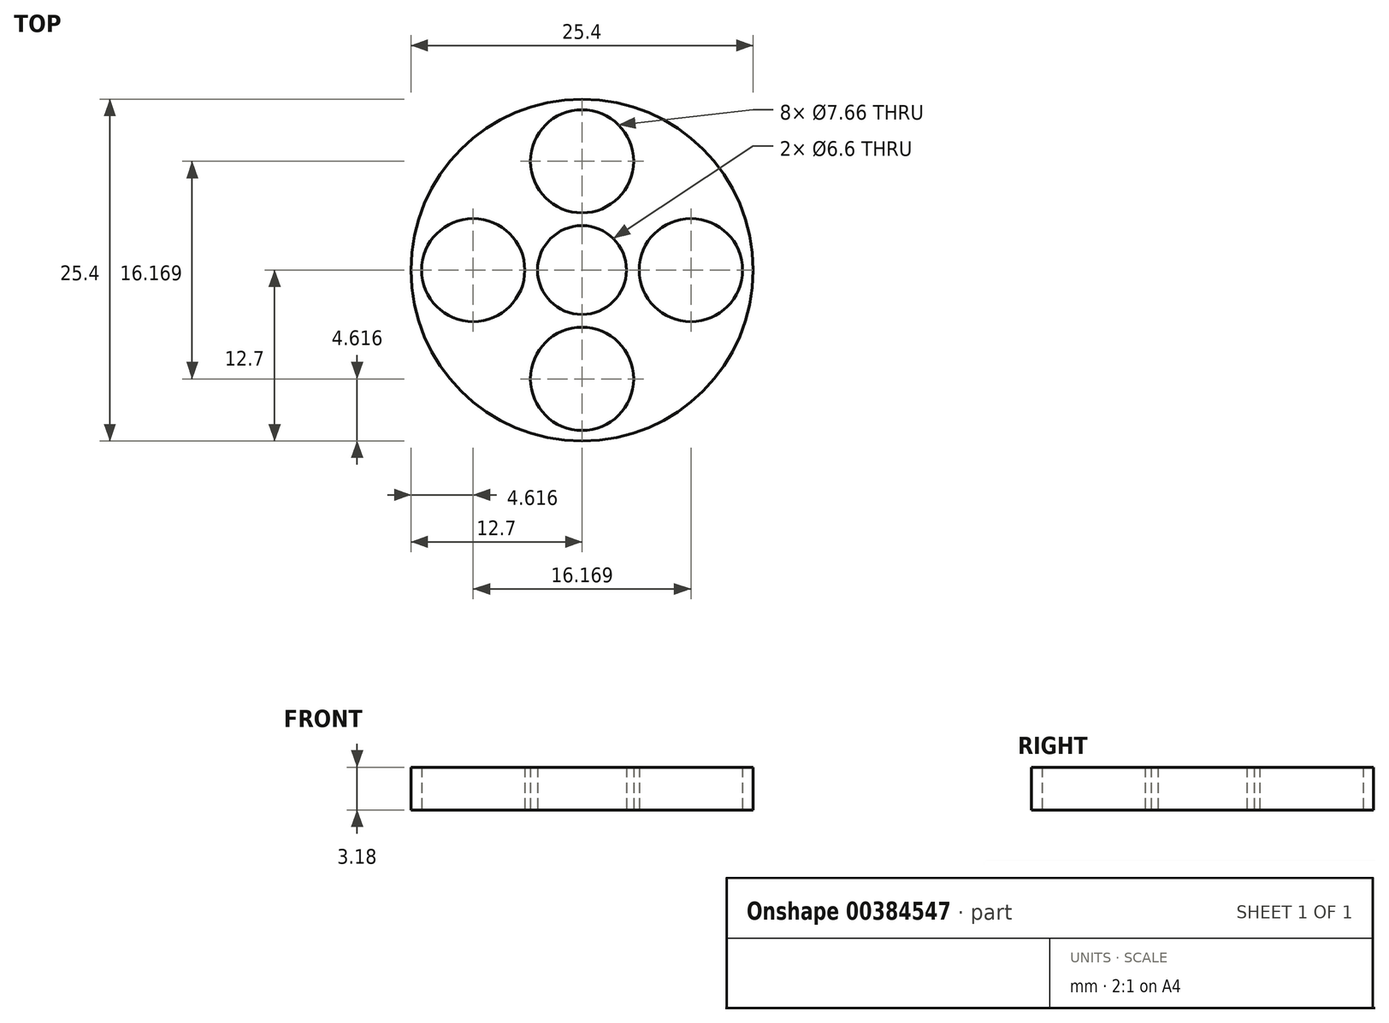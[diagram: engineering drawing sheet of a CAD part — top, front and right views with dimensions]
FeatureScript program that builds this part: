
annotation { "Feature Type Name" : "Feature", "Feature Type Description" : "" }
export const myFeature = defineFeature(function(context is Context, id is Id, definition is map)
    precondition{}
    {
        {
            var Q0;
            Q0=qCreatedBy(makeId("Top.planeOp"),FACE);
            var sketch = newSketch(context, id + "F0", { "sketchPlane" : qUnion([Q0])});
            skCircle(sketch, "E0", {"center": v(0, 0) * mm, "radius": 12.7 * mm});
            skSolve(sketch);
        }
        {
            var Q0;
            Q0=makeQuery(id+"F0.imprint","IMPRINT",FACE,{"disambiguationData":[TD([[makeQuery(id+"F0.imprint","IMPRINT",EDGE,{"derivedFrom":sQuery(id+"F0.wireOp",EDGE,"E0")}),1.0]])]});
            extrude(context, id + "F1", {"entities" : qUnion([Q0]), "depth" : 3.17 * mm});
        }
        {
            var Q0;
            Q0=qCreatedBy(makeId("Top.planeOp"),FACE);
            var sketch = newSketch(context, id + "F2", { "sketchPlane" : qUnion([Q0])});
            skCircle(sketch, "E1", {"center": v(0, 0) * mm, "radius": 3.3 * mm});
            skSolve(sketch);
        }
        {
            var Q0;
            Q0 = qSketchRegion(id + "F2", true);
            extrude(context, id + "F3", {"entities" : qUnion([Q0]), "operationType" : NewBodyOperationType.REMOVE, "depth" : 25.4 * mm});
        }
        {
            var Q0;
            Q0=qCreatedBy(makeId("Top.planeOp"),FACE);
            var sketch = newSketch(context, id + "F4", { "sketchPlane" : qUnion([Q0])});
            skCircle(sketch, "E2", {"center": v(0, 8.08) * mm, "radius": 3.83 * mm});
            skCircle(sketch, "E3.1.0", {"center": v(-8.08, 0) * mm, "radius": 3.83 * mm});
            skCircle(sketch, "E3.2.0", {"center": v(0, -8.08) * mm, "radius": 3.83 * mm});
            skCircle(sketch, "E3.3.0", {"center": v(8.08, 0) * mm, "radius": 3.83 * mm});
            skPoint(sketch, "E3.center", {"position": v(0, 0) * mm});
            skSolve(sketch);
        }
        {
            var Q0;
            Q0 = qSketchRegion(id + "F4", true);
            extrude(context, id + "F5", {"entities" : qUnion([Q0]), "operationType" : NewBodyOperationType.REMOVE, "depth" : 25.4 * mm});
        }
    });
